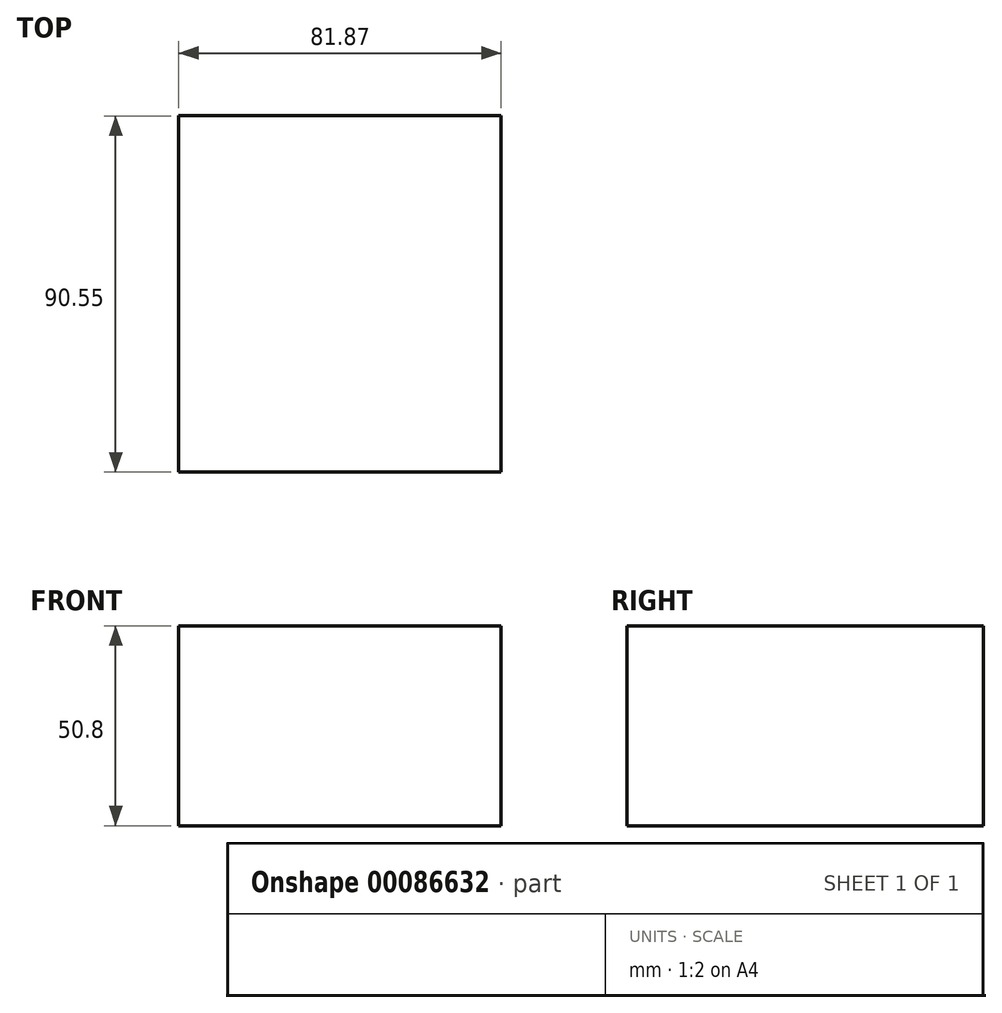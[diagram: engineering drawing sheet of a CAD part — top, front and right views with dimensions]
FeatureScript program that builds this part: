
annotation { "Feature Type Name" : "Feature", "Feature Type Description" : "" }
export const myFeature = defineFeature(function(context is Context, id is Id, definition is map)
    precondition{}
    {
        {
            var Q0;
            Q0=qCreatedBy(makeId("Top.planeOp"),FACE);
            var sketch = newSketch(context, id + "F0", { "sketchPlane" : qUnion([Q0])});
            skLineSegment(sketch, "E0", {"start": v(-102.42, -44) * mm, "end": v(-102.42, 46.55) * mm});
            skLineSegment(sketch, "E1", {"start": v(-102.42, 46.55) * mm, "end": v(-20.55, 46.55) * mm});
            skLineSegment(sketch, "E2", {"start": v(-20.55, 46.55) * mm, "end": v(-20.55, -44) * mm});
            skLineSegment(sketch, "E3", {"start": v(-20.55, -44) * mm, "end": v(-102.42, -44) * mm});
            skSolve(sketch);
        }
        {
            var Q0;
            Q0=makeQuery(id+"F0.imprint","IMPRINT",FACE,{"disambiguationData":[TD([[makeQuery(id+"F0.imprint","IMPRINT",EDGE,{"derivedFrom":sQuery(id+"F0.wireOp",EDGE,"E0")}),-1.0]])]});
            extrude(context, id + "F1", {"entities" : qUnion([Q0]), "depth" : 50.8 * mm});
        }
    });
